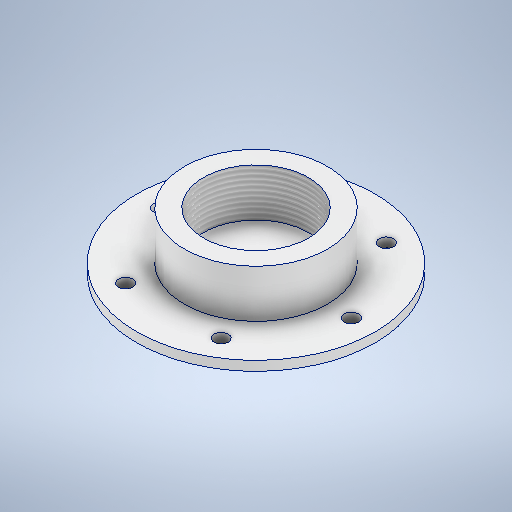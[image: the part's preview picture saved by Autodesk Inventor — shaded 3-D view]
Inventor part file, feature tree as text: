
AUTODESK INVENTOR PART (.ipt)
format: ipt  version: 2025.2 (Build 292293000, 293)  size: 303,104 bytes
history: native  units: mm
features: sketch x6, extrude x5, thread x2
ambient origin geometry x8: Origin, YZ Plane, XZ Plane, XY Plane, X Axis, Y Axis, Z Axis, Center Point
bodies: Solid1 (feature_tree)
feature tree (13):
  extrude  "Extrusion1"  Depth=5.5mm TaperAngle=0.0deg
  extrude  "Extrusion2"  Depth=2.0mm TaperAngle=0.0deg
  extrude  "Extrusion3"  Depth=10.0mm TaperAngle=0.0deg
  extrude  "Extrusion4"  TaperAngle=0.0deg  [1 undecoded]
  thread  "Thread1"  [1 undecoded]
  thread  "Thread2"  [1 undecoded]
  extrude  "Extrusion5"  Depth=3.0mm
  sketch  "Sketch1"  dims[d0=6.0mm d1=5.5mm d2=0.0mm]
  sketch  "Sketch2"  dims[d6=22.0mm d7=10.0mm d8=0.0mm]
  sketch  "Sketch3"  dims[d9=2.0mm d10=0.0mm d11=0.0mm d12=10.0mm d13=0.0mm d14=5.5mm d15=0.0mm]
  sketch  "Sketch4"  dims[d16=40.0mm d17=3.0mm]
  sketch  "Sketch5"  dims[d18=60.0mm d20=360.0deg d22=0.0mm d23=0.0mm]
  sketch  "Sketch Circular Pattern1"  dims[d3=50.0mm d4=2.0mm d5=0.0mm]
note: 3 required parameter values undecoded (feature->parameter linkage not recoverable at this tier; creation-order binding heuristic only, values carry confidence <= 0.55)
